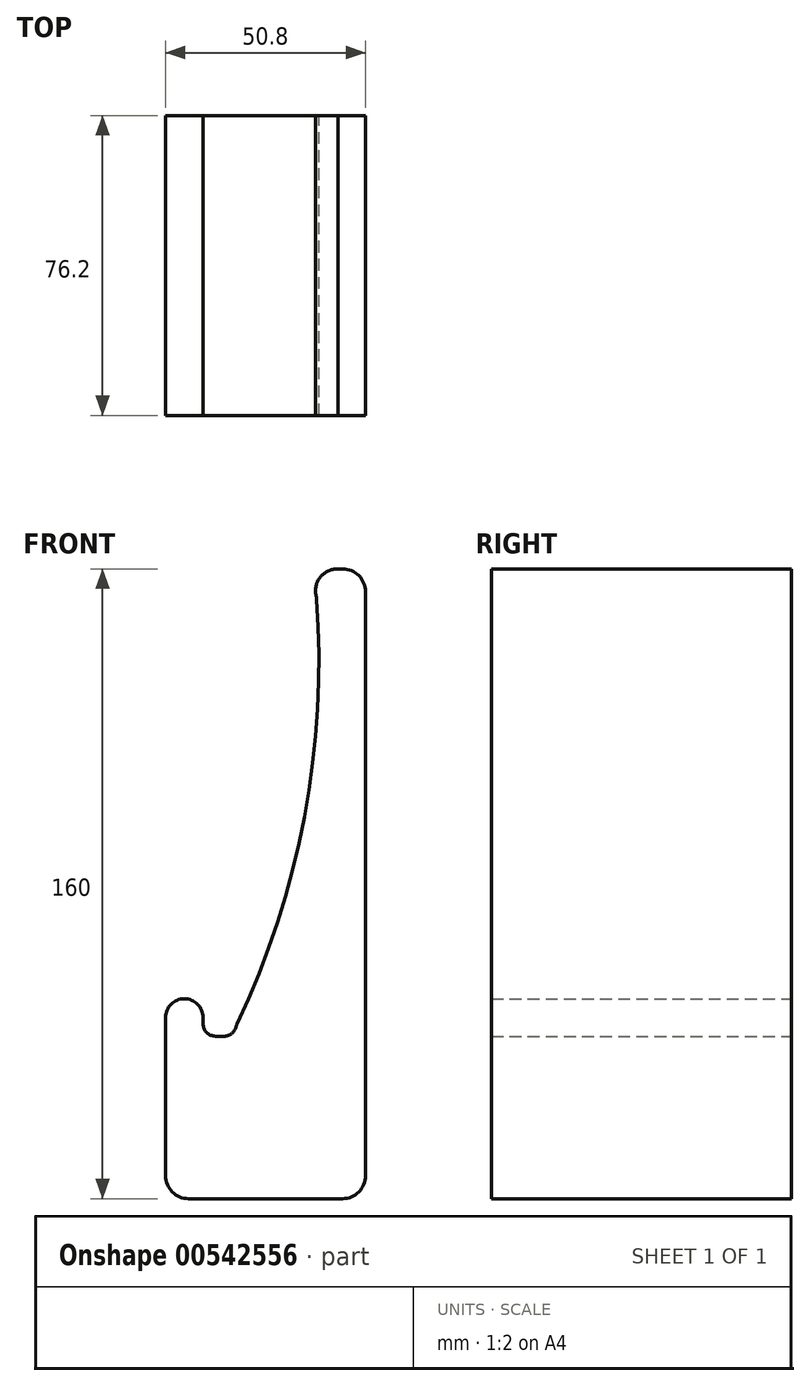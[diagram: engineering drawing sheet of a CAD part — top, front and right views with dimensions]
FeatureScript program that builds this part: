
annotation { "Feature Type Name" : "Feature", "Feature Type Description" : "" }
export const myFeature = defineFeature(function(context is Context, id is Id, definition is map)
    precondition{}
    {
        {
            var Q0;
            Q0=qCreatedBy(makeId("Front.planeOp"),FACE);
            var sketch = newSketch(context, id + "F0", { "sketchPlane" : qUnion([Q0])});
            skLineSegment(sketch, "E0", {"start": v(-25.4, -74.16) * mm, "end": v(-25.4, -33.97) * mm});
            skLineSegment(sketch, "E1", {"start": v(-15.88, -33.97) * mm, "end": v(-15.88, -35.55) * mm});
            skLineSegment(sketch, "E2", {"start": v(-12.7, -38.73) * mm, "end": v(-10.6, -38.73) * mm});
            skLineSegment(sketch, "E3", {"start": v(25.4, -74.16) * mm, "end": v(25.4, 74.16) * mm});
            skLineSegment(sketch, "E4", {"start": v(18.36, 80) * mm, "end": v(19.56, 80) * mm});
            skArc(sketch, "E5", {"start": v(-15.88, -35.55) * mm, "mid": v(-14.95, -37.8) * mm, "end": v(-12.7, -38.73) * mm});
            skArc(sketch, "E6", {"start": v(-10.6, -38.73) * mm, "mid": v(-8.69, -38.1) * mm, "end": v(-7.55, -36.45) * mm});
            skArc(sketch, "E7", {"start": v(-20.64, -29.2) * mm, "mid": v(-24, -30.6) * mm, "end": v(-25.4, -33.97) * mm});
            skArc(sketch, "E8", {"start": v(-15.88, -33.97) * mm, "mid": v(-17.27, -30.6) * mm, "end": v(-20.64, -29.2) * mm});
            skArc(sketch, "E9", {"start": v(18.36, 80) * mm, "mid": v(13.93, 77.93) * mm, "end": v(12.84, 73.15) * mm});
            skArc(sketch, "E10", {"start": v(25.4, 74.16) * mm, "mid": v(23.69, 78.3) * mm, "end": v(19.56, 80) * mm});
            skArc(sketch, "E11", {"start": v(-7.22, -35.6) * mm, "mid": v(9.87, 17) * mm, "end": v(12.99, 72.23) * mm});
            skArc(sketch, "E12", {"start": v(12.99, 72.23) * mm, "mid": v(12.93, 72.7) * mm, "end": v(12.84, 73.15) * mm});
            skArc(sketch, "E13", {"start": v(-7.55, -36.45) * mm, "mid": v(-7.4, -36.02) * mm, "end": v(-7.22, -35.6) * mm});
            skLineSegment(sketch, "E14", {"start": v(19.56, -80) * mm, "end": v(-19.56, -80) * mm});
            skArc(sketch, "E15", {"start": v(19.56, -80) * mm, "mid": v(23.69, -78.3) * mm, "end": v(25.4, -74.16) * mm});
            skArc(sketch, "E16", {"start": v(-25.4, -74.16) * mm, "mid": v(-23.69, -78.3) * mm, "end": v(-19.56, -80) * mm});
            skSolve(sketch);
        }
        {
            var Q0;
            Q0=makeQuery(id+"F0.imprint","IMPRINT",FACE,{"disambiguationData":[TD([[makeQuery(id+"F0.imprint","IMPRINT",EDGE,{"derivedFrom":sQuery(id+"F0.wireOp",EDGE,"E0")}),-1.0]])]});
            extrude(context, id + "F1", {"entities" : qUnion([Q0]), "depth" : 76.2 * mm, "offsetDistance" : 25.4 * mm});
        }
    });
